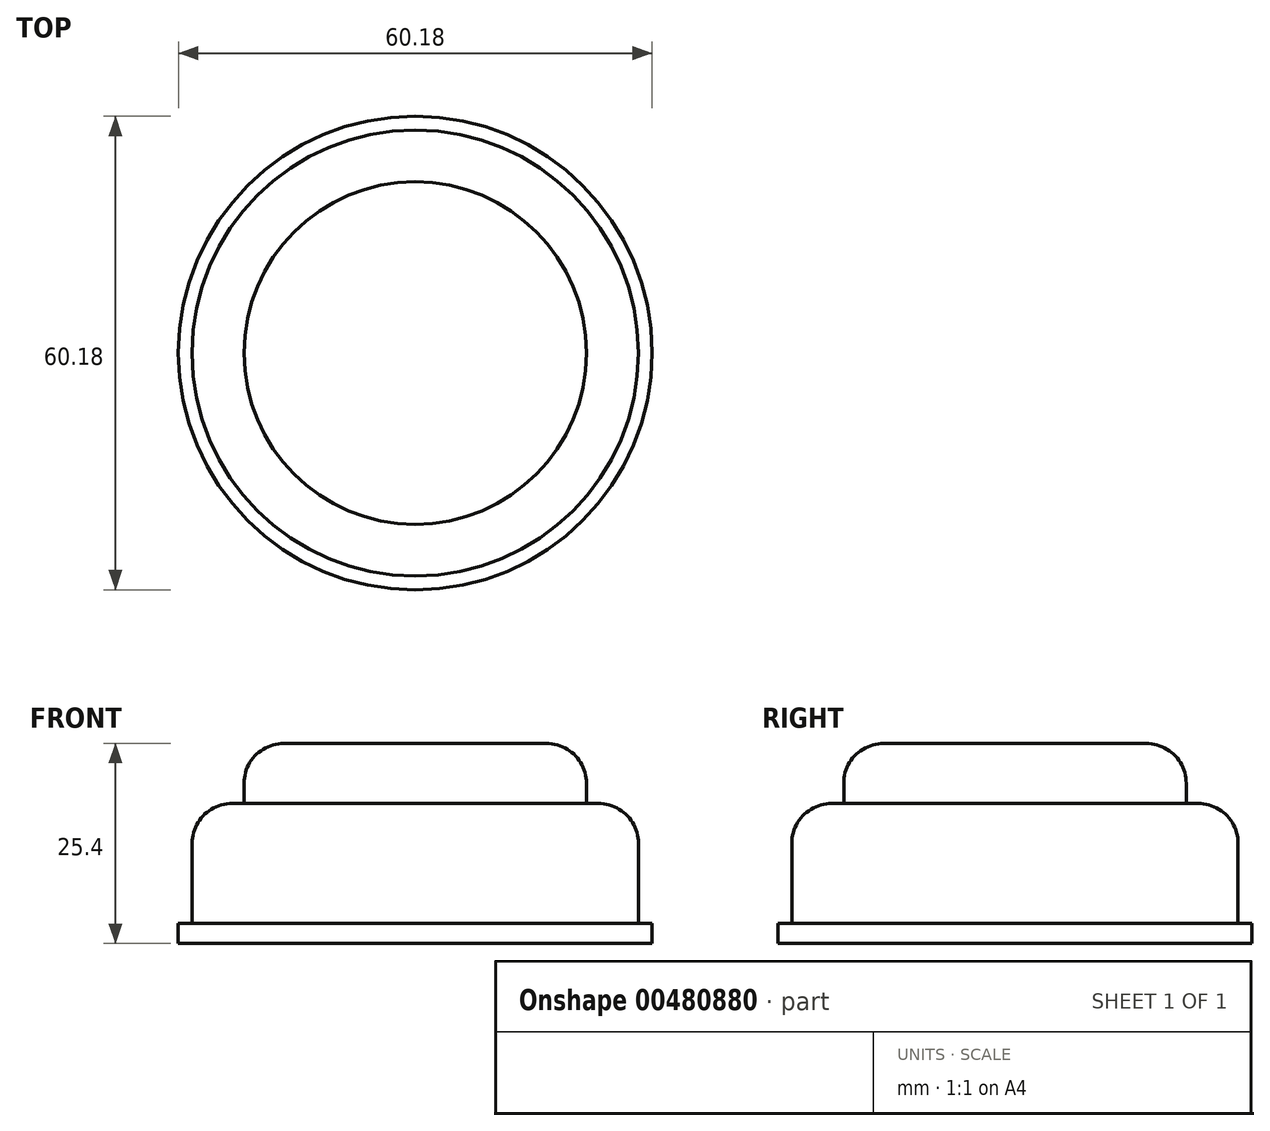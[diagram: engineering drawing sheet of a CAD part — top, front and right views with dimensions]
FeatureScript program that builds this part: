
annotation { "Feature Type Name" : "Feature", "Feature Type Description" : "" }
export const myFeature = defineFeature(function(context is Context, id is Id, definition is map)
    precondition{}
    {
        {
            var Q0;
            Q0=qCreatedBy(makeId("Top.planeOp"),FACE);
            var sketch = newSketch(context, id + "F0", { "sketchPlane" : qUnion([Q0])});
            skCircle(sketch, "E0", {"center": v(0, 0) * mm, "radius": 30.1 * mm});
            skSolve(sketch);
        }
        {
            var Q0;
            Q0 = qSketchRegion(id + "F0", true);
            extrude(context, id + "F1", {"entities" : qUnion([Q0]), "depth" : 2.54 * mm});
        }
        {
            var Q0;
            Q0=makeQuery(id+"F1.opExtrude","CAP_FACE",FACE,{"disambiguationData":[OSD([sQuery(id+"F0.wireOp",EDGE,"E0")])],"isStart":false});
            var sketch = newSketch(context, id + "F2", { "sketchPlane" : qUnion([Q0])});
            skCircle(sketch, "E1", {"center": v(0, 0) * mm, "radius": 28.34 * mm});
            skSolve(sketch);
        }
        {
            var Q0;
            Q0 = qSketchRegion(id + "F2", true);
            extrude(context, id + "F3", {"entities" : qUnion([Q0]), "operationType" : NewBodyOperationType.ADD, "depth" : 15.24 * mm});
        }
        {
            var Q0;
            Q0=makeQuery(id+"F3.opExtrude","CAP_EDGE",EDGE,{"disambiguationData":[OSD([sQuery(id+"F2.wireOp",EDGE,"E1")])],"isStart":false});
            fillet(context, id + "F4", {"entities" : qUnion([Q0]), "radius" : 5.08 * mm, "tangentPropagation" : true, "allowEdgeOverflow" : false});
        }
        {
            var Q0;
            Q0=makeQuery(id+"F3.opExtrude","CAP_FACE",FACE,{"disambiguationData":[OSD([sQuery(id+"F2.wireOp",EDGE,"E1")])],"isStart":false});
            var sketch = newSketch(context, id + "F5", { "sketchPlane" : qUnion([Q0])});
            skCircle(sketch, "E2", {"center": v(0, 0) * mm, "radius": 21.75 * mm});
            skSolve(sketch);
        }
        {
            var Q0;
            Q0 = qSketchRegion(id + "F5", true);
            extrude(context, id + "F6", {"entities" : qUnion([Q0]), "operationType" : NewBodyOperationType.ADD, "depth" : 7.62 * mm});
        }
        {
            var Q0;
            Q0=makeQuery(id+"F6.opExtrude","CAP_EDGE",EDGE,{"disambiguationData":[OSD([sQuery(id+"F5.wireOp",EDGE,"E2")])],"isStart":false});
            fillet(context, id + "F7", {"entities" : qUnion([Q0]), "radius" : 5.08 * mm, "tangentPropagation" : true, "allowEdgeOverflow" : false});
        }
    });
